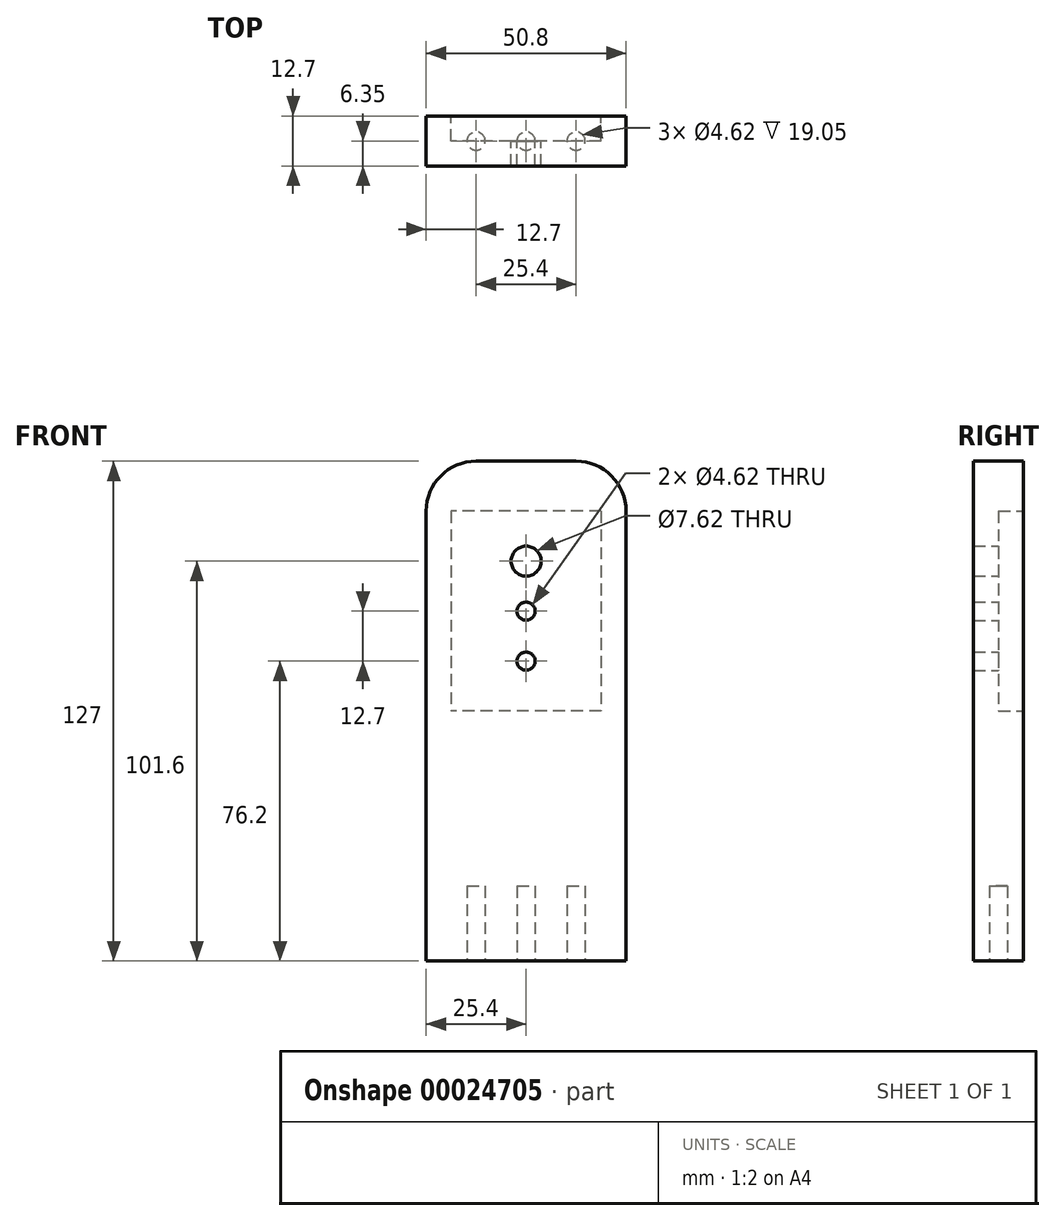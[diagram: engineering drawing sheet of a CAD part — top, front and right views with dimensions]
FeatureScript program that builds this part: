
annotation { "Feature Type Name" : "Feature", "Feature Type Description" : "" }
export const myFeature = defineFeature(function(context is Context, id is Id, definition is map)
    precondition{}
    {
        {
            var Q0;
            Q0=qCreatedBy(makeId("Top.planeOp"),FACE);
            var sketch = newSketch(context, id + "F0", { "sketchPlane" : qUnion([Q0])});
            skLineSegment(sketch, "E0.bottom", {"start": v(0, 0) * mm, "end": v(50.8, 0) * mm});
            skLineSegment(sketch, "E0.top", {"start": v(0, -12.7) * mm, "end": v(50.8, -12.7) * mm});
            skLineSegment(sketch, "E0.left", {"start": v(0, 0) * mm, "end": v(0, -12.7) * mm});
            skLineSegment(sketch, "E0.right", {"start": v(50.8, 0) * mm, "end": v(50.8, -12.7) * mm});
            skSolve(sketch);
        }
        {
            var Q0;
            Q0 = qSketchRegion(id + "F0", true);
            extrude(context, id + "F1", {"entities" : qUnion([Q0]), "depth" : 127 * mm});
        }
        {
            var Q0;
            Q0=makeQuery(id+"F1.opExtrude","CAP_FACE",FACE,{"disambiguationData":[OSD([sQuery(id+"F0.wireOp",EDGE,"E0.bottom"),sQuery(id+"F0.wireOp",EDGE,"E0.top"),sQuery(id+"F0.wireOp",EDGE,"E0.left"),sQuery(id+"F0.wireOp",EDGE,"E0.right")])],"isStart":true});
            var sketch = newSketch(context, id + "F2", { "sketchPlane" : qUnion([Q0])});
            skCircle(sketch, "E1", {"center": v(25.4, 6.35) * mm, "radius": 2.31 * mm});
            skCircle(sketch, "E2", {"center": v(38.1, 6.35) * mm, "radius": 2.31 * mm});
            skCircle(sketch, "E3", {"center": v(12.7, 6.35) * mm, "radius": 2.31 * mm});
            skSolve(sketch);
        }
        {
            var Q0;
            Q0 = qSketchRegion(id + "F2", true);
            extrude(context, id + "F3", {"entities" : qUnion([Q0]), "operationType" : NewBodyOperationType.REMOVE, "oppositeDirection" : true, "depth" : 19.05 * mm});
        }
        {
            var Q0;
            Q0=makeQuery(id+"F1.opExtrude","CAP_EDGE",EDGE,{"disambiguationData":[OSD([sQuery(id+"F0.wireOp",EDGE,"E0.right")])],"isStart":false});
            var Q1;
            Q1=makeQuery(id+"F1.opExtrude","CAP_EDGE",EDGE,{"disambiguationData":[OSD([sQuery(id+"F0.wireOp",EDGE,"E0.left")])],"isStart":false});
            fillet(context, id + "F4", {"entities" : qUnion([Q0, Q1]), "radius" : 12.7 * mm, "tangentPropagation" : true, "allowEdgeOverflow" : false});
        }
        {
            var Q0;
            Q0=makeQuery(id+"F1.opExtrude","SWEPT_FACE",FACE,{"disambiguationData":[OSD([sQuery(id+"F0.wireOp",EDGE,"E0.bottom")])]});
            var sketch = newSketch(context, id + "F5", { "sketchPlane" : qUnion([Q0])});
            skCircle(sketch, "E4", {"center": v(-25.4, 101.6) * mm, "radius": 3.81 * mm});
            skCircle(sketch, "E5", {"center": v(-25.4, 88.9) * mm, "radius": 2.31 * mm});
            skCircle(sketch, "E6", {"center": v(-25.4, 76.2) * mm, "radius": 2.31 * mm});
            skSolve(sketch);
        }
        {
            var Q0;
            Q0 = qSketchRegion(id + "F5", true);
            extrude(context, id + "F6", {"entities" : qUnion([Q0]), "operationType" : NewBodyOperationType.REMOVE, "oppositeDirection" : true, "depth" : 25.4 * mm});
        }
        {
            var Q0;
            Q0=makeQuery(id+"F1.opExtrude","SWEPT_FACE",FACE,{"disambiguationData":[OSD([sQuery(id+"F0.wireOp",EDGE,"E0.bottom")])]});
            var sketch = newSketch(context, id + "F7", { "sketchPlane" : qUnion([Q0])});
            skLineSegment(sketch, "E7", {"start": v(-50.8, 114.3) * mm, "end": v(0, 114.3) * mm});
            skLineSegment(sketch, "E8.bottom", {"start": v(-44.45, 114.3) * mm, "end": v(-6.35, 114.3) * mm});
            skLineSegment(sketch, "E8.top", {"start": v(-44.45, 63.5) * mm, "end": v(-6.35, 63.5) * mm});
            skLineSegment(sketch, "E8.left", {"start": v(-44.45, 114.3) * mm, "end": v(-44.45, 63.5) * mm});
            skLineSegment(sketch, "E8.right", {"start": v(-6.35, 114.3) * mm, "end": v(-6.35, 63.5) * mm});
            skSolve(sketch);
        }
        {
            var Q0;
            Q0 = qSketchRegion(id + "F7", true);
            extrude(context, id + "F8", {"entities" : qUnion([Q0]), "operationType" : NewBodyOperationType.REMOVE, "oppositeDirection" : true, "depth" : 6.35 * mm});
        }
    });
